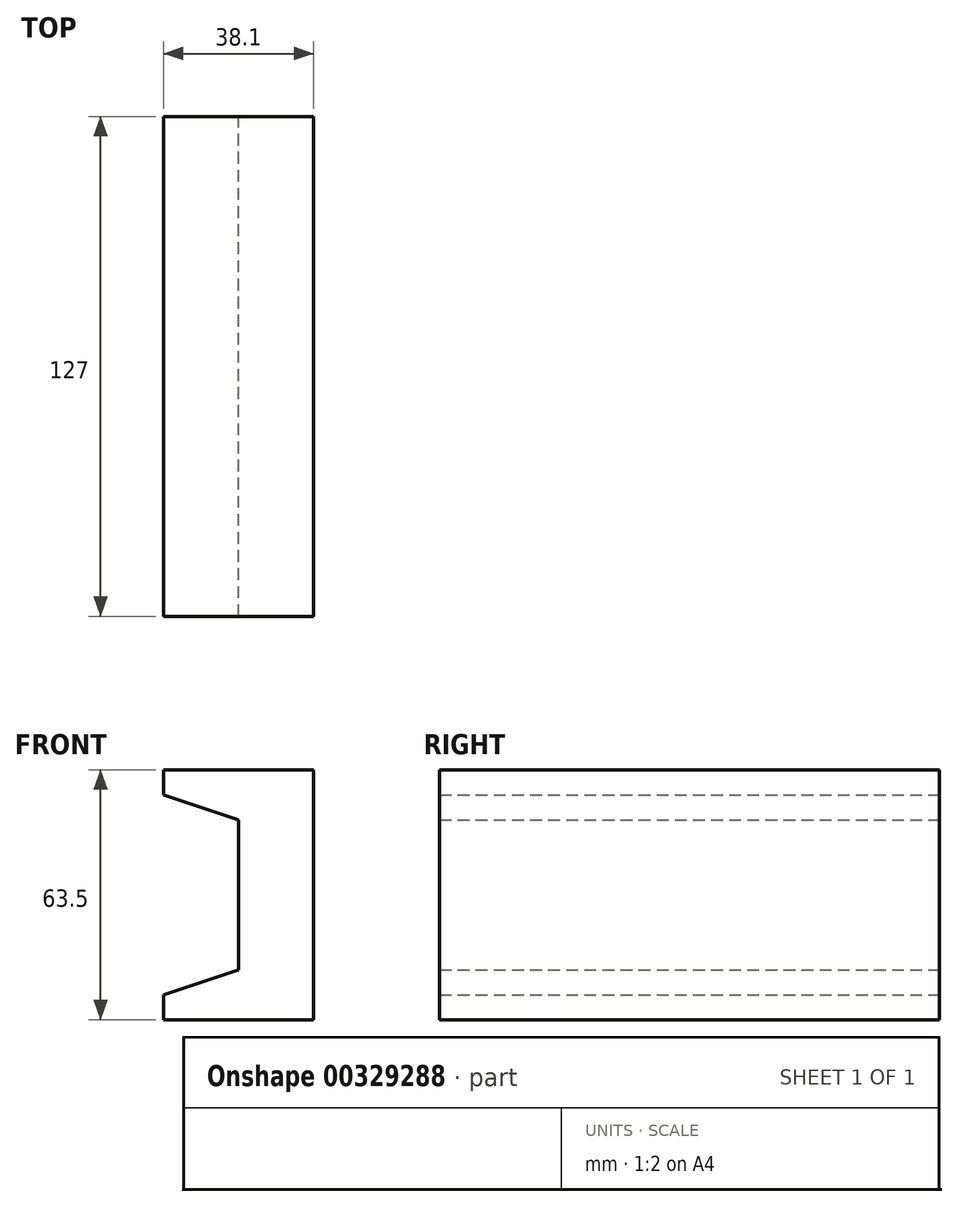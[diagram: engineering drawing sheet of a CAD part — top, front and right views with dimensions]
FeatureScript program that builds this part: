
annotation { "Feature Type Name" : "Feature", "Feature Type Description" : "" }
export const myFeature = defineFeature(function(context is Context, id is Id, definition is map)
    precondition{}
    {
        {
            var Q0;
            Q0=qCreatedBy(makeId("Front.planeOp"),FACE);
            var sketch = newSketch(context, id + "F0", { "sketchPlane" : qUnion([Q0])});
            skLineSegment(sketch, "E0", {"start": v(44.45, -32.02) * mm, "end": v(44.45, 31.48) * mm});
            skLineSegment(sketch, "E1", {"start": v(44.45, 31.48) * mm, "end": v(6.35, 31.48) * mm});
            skLineSegment(sketch, "E2", {"start": v(44.45, -32.02) * mm, "end": v(6.35, -32.02) * mm});
            skLineSegment(sketch, "E3", {"start": v(6.35, 31.48) * mm, "end": v(6.35, 25.13) * mm});
            skLineSegment(sketch, "E4", {"start": v(6.35, -32.02) * mm, "end": v(6.35, -25.67) * mm});
            skPoint(sketch, "E5.orphan", {"position": v(25.4, -32.02) * mm});
            skLineSegment(sketch, "E6", {"start": v(25.4, -19.32) * mm, "end": v(25.4, 18.78) * mm});
            skLineSegment(sketch, "E7", {"start": v(6.35, 25.13) * mm, "end": v(25.4, 18.78) * mm});
            skPoint(sketch, "E8.orphan", {"position": v(25.4, 31.48) * mm});
            skLineSegment(sketch, "E9", {"start": v(6.35, -25.67) * mm, "end": v(25.4, -19.32) * mm});
            skSolve(sketch);
        }
        {
            var Q0;
            Q0 = qSketchRegion(id + "F0", true);
            extrude(context, id + "F1", {"entities" : qUnion([Q0]), "depth" : 127 * mm});
        }
    });
